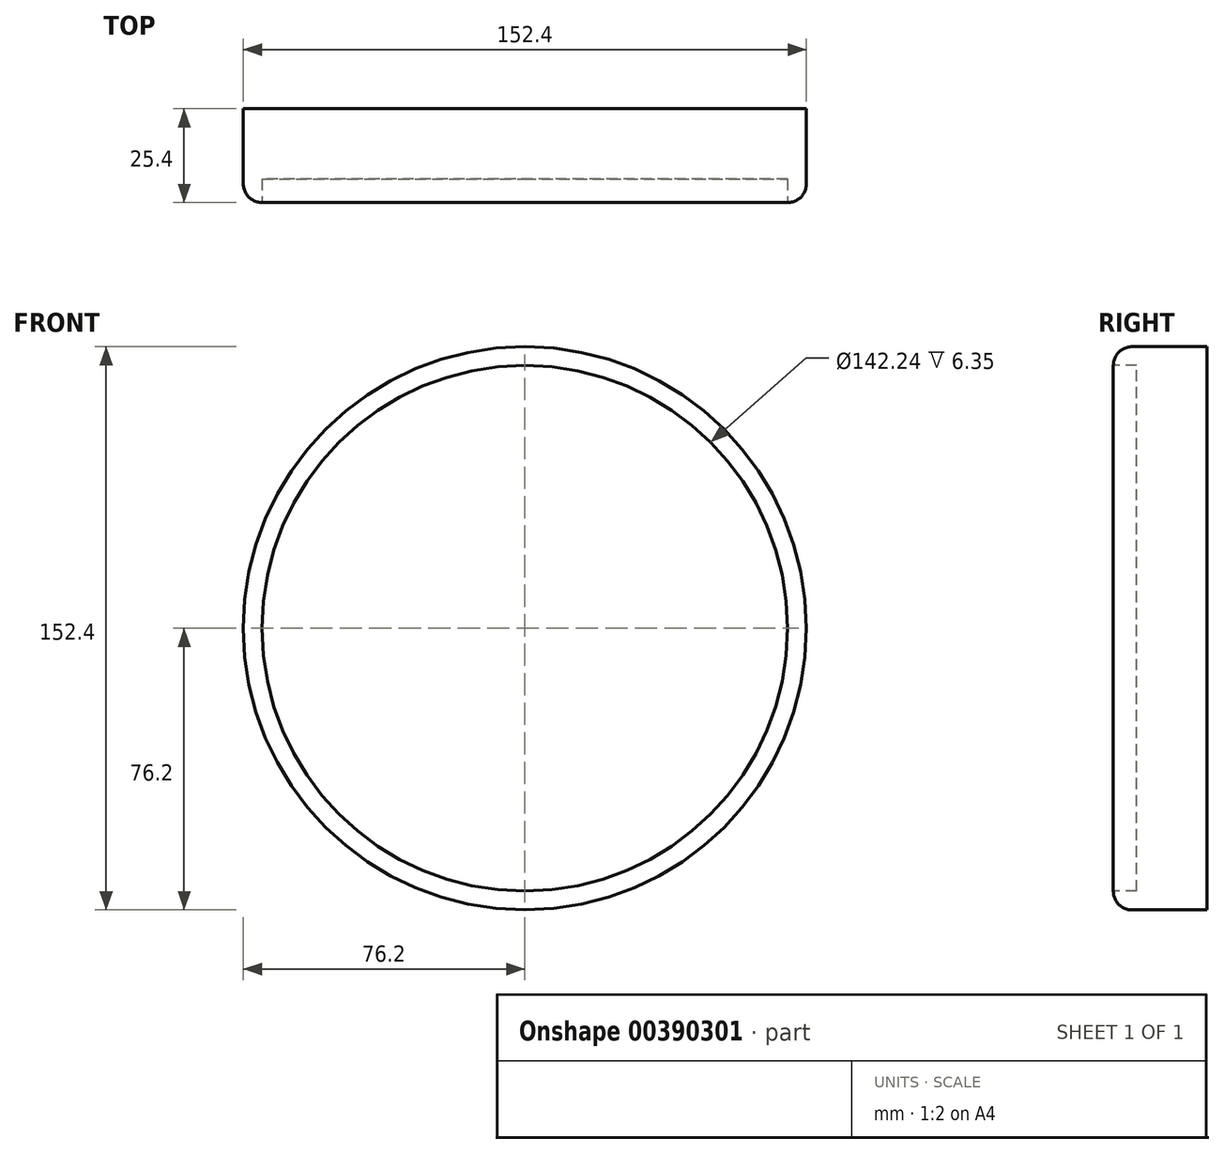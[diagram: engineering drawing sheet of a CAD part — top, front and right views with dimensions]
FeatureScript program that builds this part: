
annotation { "Feature Type Name" : "Feature", "Feature Type Description" : "" }
export const myFeature = defineFeature(function(context is Context, id is Id, definition is map)
    precondition{}
    {
        {
            var Q0;
            Q0=qCreatedBy(makeId("Front.planeOp"),FACE);
            var sketch = newSketch(context, id + "F0", { "sketchPlane" : qUnion([Q0])});
            skCircle(sketch, "E0", {"center": v(0, 0) * mm, "radius": 76.2 * mm});
            skSolve(sketch);
        }
        {
            var Q0;
            Q0=makeQuery(id+"F0.imprint","IMPRINT",FACE,{"disambiguationData":[TD([[makeQuery(id+"F0.imprint","IMPRINT",EDGE,{"derivedFrom":sQuery(id+"F0.wireOp",EDGE,"E0")}),1.0]])]});
            extrude(context, id + "F1", {"entities" : qUnion([Q0]), "depth" : 25.4 * mm});
        }
        {
            var Q0;
            Q0=makeQuery(id+"F1.opExtrude","CAP_EDGE",EDGE,{"disambiguationData":[OSD([sQuery(id+"F0.wireOp",EDGE,"E0")])],"isStart":false});
            fillet(context, id + "F2", {"entities" : qUnion([Q0]), "radius" : 5.08 * mm, "tangentPropagation" : true, "allowEdgeOverflow" : false});
        }
        {
            var Q0;
            Q0=makeQuery(id+"F1.opExtrude","CAP_FACE",FACE,{"disambiguationData":[OSD([sQuery(id+"F0.wireOp",EDGE,"E0")])],"isStart":false});
            extrude(context, id + "F3", {"entities" : qUnion([Q0]), "operationType" : NewBodyOperationType.REMOVE, "oppositeDirection" : true, "depth" : 6.35 * mm});
        }
    });
